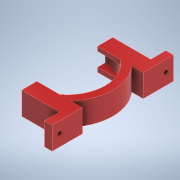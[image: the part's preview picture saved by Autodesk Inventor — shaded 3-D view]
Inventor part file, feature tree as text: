
AUTODESK INVENTOR PART (.ipt)
format: ipt  version: 2022.2 (Build 262287010, 287A)  size: 165,376 bytes
history: native  units: in
note: dims shown in document units (in); Inventor stores cm internally (conversion verified against a paired STEP export)
features: extrude x5, sketch x5, mirror x3, other x1
ambient origin geometry x8: Origin, YZ Plane, XZ Plane, XY Plane, X Axis, Y Axis, Z Axis, Center Point
bodies: Body1 (feature_tree)
feature tree (14):
  other  "Sólido1"
  extrude  "Extrusión1"  Depth=0.1969in
  extrude  "Extrusión2"  Depth=0.5906in TaperAngle=0.0deg
  mirror  "Simetría1"
  extrude  "Extrusión3"  Depth=0.1161in TaperAngle=0.0deg
  mirror  "Simetría2"
  extrude  "Extrusión4"  Depth=0.1969in
  extrude  "Extrusión5"  Depth=0.3937in
  mirror  "Simetría3"
  sketch  "Boceto1"  dims[d0=1.9783in d1=0.1969in]
  sketch  "Boceto2"  dims[d2=0.3937in d3=0.5906in d4=0.0in]
  sketch  "Boceto3"  dims[d5=0.1969in d6=0.1161in d7=0.0in]
  sketch  "Boceto4"  dims[d8=0.1161in d9=0.0in d10=0.1969in]
  sketch  "Boceto5"  dims[d11=0.3937in d12=0.0in d13=0.1181in d14=0.3937in d15=0.0in d17=0.0197in d18=0.0344in d19=0.0197in d20=0.0344in]
